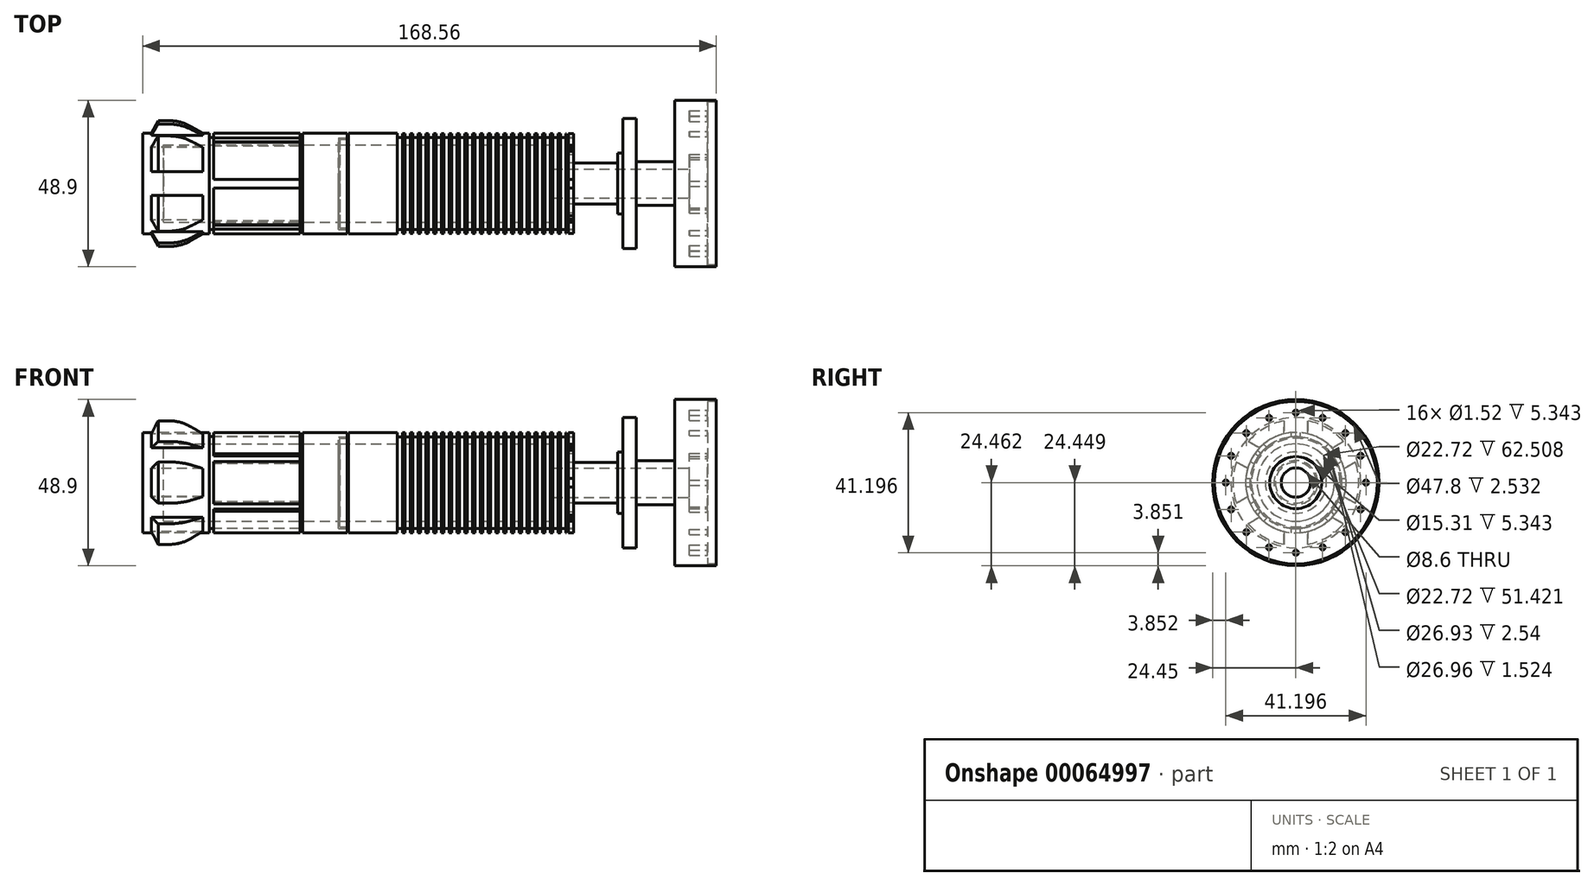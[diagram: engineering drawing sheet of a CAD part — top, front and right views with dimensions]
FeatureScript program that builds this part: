
annotation { "Feature Type Name" : "Feature", "Feature Type Description" : "" }
export const myFeature = defineFeature(function(context is Context, id is Id, definition is map)
    precondition{}
    {
        {
            var Q0;
            Q0=qCreatedBy(makeId("Front.planeOp"),FACE);
            var sketch = newSketch(context, id + "F0", { "sketchPlane" : qUnion([Q0])});
            skLineSegment(sketch, "E0", {"start": v(-51.18, 19.75) * mm, "end": v(-48.64, 19.75) * mm});
            skLineSegment(sketch, "E1", {"start": v(73.35, 19.75) * mm, "end": v(73.35, 28.51) * mm});
            skLineSegment(sketch, "E2", {"start": v(73.35, 28.51) * mm, "end": v(88.38, 28.51) * mm});
            skLineSegment(sketch, "E3", {"start": v(88.38, 28.51) * mm, "end": v(88.38, 25.51) * mm});
            skLineSegment(sketch, "E4", {"start": v(88.38, 25.51) * mm, "end": v(90, 25.51) * mm});
            skLineSegment(sketch, "E5", {"start": v(90, 25.51) * mm, "end": v(90, 15.36) * mm});
            skLineSegment(sketch, "E6", {"start": v(90, 15.36) * mm, "end": v(93.92, 15.36) * mm});
            skLineSegment(sketch, "E7", {"start": v(93.92, 15.36) * mm, "end": v(93.92, 28.05) * mm});
            skLineSegment(sketch, "E8", {"start": v(93.92, 28.05) * mm, "end": v(105.22, 28.05) * mm});
            skLineSegment(sketch, "E9", {"start": v(105.22, 28.05) * mm, "end": v(105.22, 10.06) * mm});
            skLineSegment(sketch, "E10", {"start": v(105.22, 10.06) * mm, "end": v(114.85, 10.06) * mm});
            skLineSegment(sketch, "E11", {"start": v(114.85, 10.6) * mm, "end": v(114.85, 27) * mm});
            skLineSegment(sketch, "E12", {"start": v(-51.18, 19.75) * mm, "end": v(-51.18, 28.51) * mm});
            skLineSegment(sketch, "E13", {"start": v(-51.18, 28.51) * mm, "end": v(-51.18, 34.5) * mm});
            skLineSegment(sketch, "E14", {"start": v(-51.18, 34.5) * mm, "end": v(114.85, 34.5) * mm});
            skLineSegment(sketch, "E15", {"start": v(114.85, 34.5) * mm, "end": v(114.85, 27) * mm});
            skLineSegment(sketch, "E16", {"start": v(114.85, 10.06) * mm, "end": v(117.38, 10.06) * mm});
            skLineSegment(sketch, "E17", {"start": v(117.38, 10.06) * mm, "end": v(117.38, 10.6) * mm});
            skLineSegment(sketch, "E18", {"start": v(117.38, 10.6) * mm, "end": v(114.85, 10.6) * mm});
            skLineSegment(sketch, "E19", {"start": v(-48.64, 19.75) * mm, "end": v(-46.64, 16.02) * mm});
            skLineSegment(sketch, "E20", {"start": v(-46.64, 16.02) * mm, "end": v(-39.86, 16.02) * mm});
            skLineSegment(sketch, "E21", {"start": v(-39.86, 16.02) * mm, "end": v(-33.55, 19.75) * mm});
            skLineSegment(sketch, "E22.trimOffspring", {"start": v(-33.55, 19.75) * mm, "end": v(-31.55, 19.75) * mm});
            skLineSegment(sketch, "E23", {"start": v(77.77, 19.75) * mm, "end": v(77.77, 21.03) * mm});
            skLineSegment(sketch, "E24", {"start": v(77.77, 21.03) * mm, "end": v(76.24, 21.03) * mm});
            skLineSegment(sketch, "E25", {"start": v(76.24, 21.03) * mm, "end": v(76.24, 19.75) * mm});
            skLineSegment(sketch, "E26.1.0.0", {"start": v(75.48, 19.75) * mm, "end": v(75.48, 21.03) * mm});
            skLineSegment(sketch, "E26.1.0.1", {"start": v(75.48, 21.03) * mm, "end": v(73.96, 21.03) * mm});
            skLineSegment(sketch, "E26.1.0.2", {"start": v(73.96, 21.03) * mm, "end": v(73.96, 19.75) * mm});
            skLineSegment(sketch, "E26.2.0.0", {"start": v(73.2, 19.75) * mm, "end": v(73.2, 21.03) * mm});
            skLineSegment(sketch, "E26.2.0.1", {"start": v(73.2, 21.03) * mm, "end": v(71.67, 21.03) * mm});
            skLineSegment(sketch, "E26.2.0.2", {"start": v(71.67, 21.03) * mm, "end": v(71.67, 19.75) * mm});
            skLineSegment(sketch, "E26.3.0.0", {"start": v(70.9, 19.75) * mm, "end": v(70.9, 21.03) * mm});
            skLineSegment(sketch, "E26.3.0.1", {"start": v(70.9, 21.03) * mm, "end": v(69.39, 21.03) * mm});
            skLineSegment(sketch, "E26.3.0.2", {"start": v(69.39, 21.03) * mm, "end": v(69.39, 19.75) * mm});
            skLineSegment(sketch, "E26.4.0.0", {"start": v(68.62, 19.75) * mm, "end": v(68.62, 21.03) * mm});
            skLineSegment(sketch, "E26.4.0.1", {"start": v(68.62, 21.03) * mm, "end": v(67.1, 21.03) * mm});
            skLineSegment(sketch, "E26.4.0.2", {"start": v(67.1, 21.03) * mm, "end": v(67.1, 19.75) * mm});
            skLineSegment(sketch, "E26.5.0.0", {"start": v(66.34, 19.75) * mm, "end": v(66.34, 21.03) * mm});
            skLineSegment(sketch, "E26.5.0.1", {"start": v(66.34, 21.03) * mm, "end": v(64.81, 21.03) * mm});
            skLineSegment(sketch, "E26.5.0.2", {"start": v(64.81, 21.03) * mm, "end": v(64.81, 19.75) * mm});
            skLineSegment(sketch, "E26.6.0.0", {"start": v(64.05, 19.75) * mm, "end": v(64.05, 21.03) * mm});
            skLineSegment(sketch, "E26.6.0.1", {"start": v(64.05, 21.03) * mm, "end": v(62.53, 21.03) * mm});
            skLineSegment(sketch, "E26.6.0.2", {"start": v(62.53, 21.03) * mm, "end": v(62.53, 19.75) * mm});
            skLineSegment(sketch, "E26.7.0.0", {"start": v(61.77, 19.75) * mm, "end": v(61.77, 21.03) * mm});
            skLineSegment(sketch, "E26.7.0.1", {"start": v(61.77, 21.03) * mm, "end": v(60.24, 21.03) * mm});
            skLineSegment(sketch, "E26.7.0.2", {"start": v(60.24, 21.03) * mm, "end": v(60.24, 19.75) * mm});
            skLineSegment(sketch, "E26.8.0.0", {"start": v(59.48, 19.75) * mm, "end": v(59.48, 21.03) * mm});
            skLineSegment(sketch, "E26.8.0.1", {"start": v(59.48, 21.03) * mm, "end": v(57.96, 21.03) * mm});
            skLineSegment(sketch, "E26.8.0.2", {"start": v(57.96, 21.03) * mm, "end": v(57.96, 19.75) * mm});
            skLineSegment(sketch, "E26.9.0.0", {"start": v(57.2, 19.75) * mm, "end": v(57.2, 21.03) * mm});
            skLineSegment(sketch, "E26.9.0.1", {"start": v(57.2, 21.03) * mm, "end": v(55.67, 21.03) * mm});
            skLineSegment(sketch, "E26.9.0.2", {"start": v(55.67, 21.03) * mm, "end": v(55.67, 19.75) * mm});
            skLineSegment(sketch, "E26.10.0.0", {"start": v(54.9, 19.75) * mm, "end": v(54.9, 21.03) * mm});
            skLineSegment(sketch, "E26.10.0.1", {"start": v(54.9, 21.03) * mm, "end": v(53.38, 21.03) * mm});
            skLineSegment(sketch, "E26.10.0.2", {"start": v(53.38, 21.03) * mm, "end": v(53.38, 19.75) * mm});
            skLineSegment(sketch, "E26.11.0.0", {"start": v(52.62, 19.75) * mm, "end": v(52.62, 21.03) * mm});
            skLineSegment(sketch, "E26.11.0.1", {"start": v(52.62, 21.03) * mm, "end": v(51.1, 21.03) * mm});
            skLineSegment(sketch, "E26.11.0.2", {"start": v(51.1, 21.03) * mm, "end": v(51.1, 19.75) * mm});
            skLineSegment(sketch, "E26.direction1", {"start": v(76.24, 19.75) * mm, "end": v(75.48, 19.75) * mm, "construction": true});
            skLineSegment(sketch, "E27.0.12.0", {"start": v(50.34, 19.75) * mm, "end": v(50.34, 21.03) * mm});
            skLineSegment(sketch, "E27.3.12.0", {"start": v(50.34, 21.03) * mm, "end": v(48.81, 21.03) * mm});
            skLineSegment(sketch, "E27.6.12.0", {"start": v(48.81, 21.03) * mm, "end": v(48.81, 19.75) * mm});
            skLineSegment(sketch, "E27.0.13.0", {"start": v(48.05, 19.75) * mm, "end": v(48.05, 21.03) * mm});
            skLineSegment(sketch, "E27.3.13.0", {"start": v(48.05, 21.03) * mm, "end": v(46.53, 21.03) * mm});
            skLineSegment(sketch, "E27.6.13.0", {"start": v(46.53, 21.03) * mm, "end": v(46.53, 19.75) * mm});
            skLineSegment(sketch, "E27.0.14.0", {"start": v(45.76, 19.75) * mm, "end": v(45.76, 21.03) * mm});
            skLineSegment(sketch, "E27.3.14.0", {"start": v(45.76, 21.03) * mm, "end": v(44.24, 21.03) * mm});
            skLineSegment(sketch, "E27.6.14.0", {"start": v(44.24, 21.03) * mm, "end": v(44.24, 19.75) * mm});
            skLineSegment(sketch, "E27.0.15.0", {"start": v(43.48, 19.75) * mm, "end": v(43.48, 21.03) * mm});
            skLineSegment(sketch, "E27.3.15.0", {"start": v(43.48, 21.03) * mm, "end": v(41.95, 21.03) * mm});
            skLineSegment(sketch, "E27.6.15.0", {"start": v(41.95, 21.03) * mm, "end": v(41.95, 19.75) * mm});
            skLineSegment(sketch, "E27.0.16.0", {"start": v(41.2, 19.75) * mm, "end": v(41.2, 21.03) * mm});
            skLineSegment(sketch, "E27.3.16.0", {"start": v(41.2, 21.03) * mm, "end": v(39.67, 21.03) * mm});
            skLineSegment(sketch, "E27.6.16.0", {"start": v(39.67, 21.03) * mm, "end": v(39.67, 19.75) * mm});
            skLineSegment(sketch, "E27.0.17.0", {"start": v(38.9, 19.75) * mm, "end": v(38.9, 21.03) * mm});
            skLineSegment(sketch, "E27.3.17.0", {"start": v(38.9, 21.03) * mm, "end": v(37.38, 21.03) * mm});
            skLineSegment(sketch, "E27.6.17.0", {"start": v(37.38, 21.03) * mm, "end": v(37.38, 19.75) * mm});
            skLineSegment(sketch, "E27.0.18.0", {"start": v(36.62, 19.75) * mm, "end": v(36.62, 21.03) * mm});
            skLineSegment(sketch, "E27.3.18.0", {"start": v(36.62, 21.03) * mm, "end": v(35.1, 21.03) * mm});
            skLineSegment(sketch, "E27.6.18.0", {"start": v(35.1, 21.03) * mm, "end": v(35.1, 19.75) * mm});
            skLineSegment(sketch, "E27.0.19.0", {"start": v(34.33, 19.75) * mm, "end": v(34.33, 21.03) * mm});
            skLineSegment(sketch, "E27.3.19.0", {"start": v(34.33, 21.03) * mm, "end": v(32.8, 21.03) * mm});
            skLineSegment(sketch, "E27.6.19.0", {"start": v(32.8, 21.03) * mm, "end": v(32.8, 19.75) * mm});
            skLineSegment(sketch, "E28.0.20.0", {"start": v(32.05, 19.75) * mm, "end": v(32.05, 21.03) * mm});
            skLineSegment(sketch, "E28.3.20.0", {"start": v(32.05, 21.03) * mm, "end": v(30.52, 21.03) * mm});
            skLineSegment(sketch, "E28.6.20.0", {"start": v(30.52, 21.03) * mm, "end": v(30.52, 19.75) * mm});
            skLineSegment(sketch, "E28.0.21.0", {"start": v(29.76, 19.75) * mm, "end": v(29.76, 21.03) * mm});
            skLineSegment(sketch, "E28.3.21.0", {"start": v(29.76, 21.03) * mm, "end": v(28.24, 21.03) * mm});
            skLineSegment(sketch, "E28.6.21.0", {"start": v(28.24, 21.03) * mm, "end": v(28.24, 19.75) * mm});
            skLineSegment(sketch, "E28.0.22.0", {"start": v(27.48, 19.75) * mm, "end": v(27.48, 21.03) * mm});
            skLineSegment(sketch, "E28.3.22.0", {"start": v(27.48, 21.03) * mm, "end": v(25.95, 21.03) * mm});
            skLineSegment(sketch, "E28.6.22.0", {"start": v(25.95, 21.03) * mm, "end": v(25.95, 19.75) * mm});
            skLineSegment(sketch, "E28.0.23.0", {"start": v(25.19, 19.75) * mm, "end": v(25.19, 21.03) * mm});
            skLineSegment(sketch, "E28.3.23.0", {"start": v(25.19, 21.03) * mm, "end": v(23.67, 21.03) * mm});
            skLineSegment(sketch, "E28.6.23.0", {"start": v(23.67, 21.03) * mm, "end": v(23.67, 19.75) * mm});
            skLineSegment(sketch, "E29.trimOffspring", {"start": v(73.35, 19.75) * mm, "end": v(77.77, 19.75) * mm});
            skLineSegment(sketch, "E30.trimOffspring", {"start": v(75.48, 19.75) * mm, "end": v(76.24, 19.75) * mm});
            skLineSegment(sketch, "E31.trimOffspring", {"start": v(73.2, 19.75) * mm, "end": v(73.96, 19.75) * mm});
            skLineSegment(sketch, "E32.trimOffspring", {"start": v(70.9, 19.75) * mm, "end": v(71.67, 19.75) * mm});
            skLineSegment(sketch, "E33.trimOffspring", {"start": v(68.62, 19.75) * mm, "end": v(69.39, 19.75) * mm});
            skLineSegment(sketch, "E34.trimOffspring", {"start": v(66.34, 19.75) * mm, "end": v(67.1, 19.75) * mm});
            skLineSegment(sketch, "E35.trimOffspring", {"start": v(64.05, 19.75) * mm, "end": v(64.81, 19.75) * mm});
            skLineSegment(sketch, "E36.trimOffspring", {"start": v(61.77, 19.75) * mm, "end": v(62.53, 19.75) * mm});
            skLineSegment(sketch, "E37.trimOffspring", {"start": v(59.48, 19.75) * mm, "end": v(60.24, 19.75) * mm});
            skLineSegment(sketch, "E38.trimOffspring", {"start": v(57.2, 19.75) * mm, "end": v(57.96, 19.75) * mm});
            skLineSegment(sketch, "E39.trimOffspring", {"start": v(52.62, 19.75) * mm, "end": v(53.38, 19.75) * mm});
            skLineSegment(sketch, "E40.trimOffspring", {"start": v(50.34, 19.75) * mm, "end": v(51.1, 19.75) * mm});
            skLineSegment(sketch, "E41.trimOffspring", {"start": v(48.05, 19.75) * mm, "end": v(48.81, 19.75) * mm});
            skLineSegment(sketch, "E42.trimOffspring", {"start": v(45.76, 19.75) * mm, "end": v(46.53, 19.75) * mm});
            skLineSegment(sketch, "E43.trimOffspring", {"start": v(43.48, 19.75) * mm, "end": v(44.24, 19.75) * mm});
            skLineSegment(sketch, "E44.trimOffspring", {"start": v(25.19, 19.75) * mm, "end": v(25.95, 19.75) * mm});
            skLineSegment(sketch, "E45.trimOffspring", {"start": v(27.48, 19.75) * mm, "end": v(28.24, 19.75) * mm});
            skLineSegment(sketch, "E46.trimOffspring", {"start": v(29.76, 19.75) * mm, "end": v(30.52, 19.75) * mm});
            skLineSegment(sketch, "E47.trimOffspring", {"start": v(34.33, 19.75) * mm, "end": v(35.1, 19.75) * mm});
            skLineSegment(sketch, "E48.trimOffspring", {"start": v(36.62, 19.75) * mm, "end": v(37.38, 19.75) * mm});
            skLineSegment(sketch, "E49.trimOffspring", {"start": v(38.9, 19.75) * mm, "end": v(39.67, 19.75) * mm});
            skLineSegment(sketch, "E50.trimOffspring", {"start": v(41.2, 19.75) * mm, "end": v(41.95, 19.75) * mm});
            skLineSegment(sketch, "E51", {"start": v(54.9, 19.75) * mm, "end": v(55.67, 19.75) * mm});
            skLineSegment(sketch, "E52", {"start": v(32.8, 19.75) * mm, "end": v(32.05, 19.75) * mm});
            skLineSegment(sketch, "E53.top", {"start": v(-31.55, 21.01) * mm, "end": v(-30.34, 21.01) * mm});
            skLineSegment(sketch, "E53.left", {"start": v(-31.55, 19.75) * mm, "end": v(-31.55, 21.01) * mm});
            skLineSegment(sketch, "E53.right", {"start": v(-30.34, 19.75) * mm, "end": v(-30.34, 21.01) * mm});
            skPoint(sketch, "E54.oppositeSnap0", {"position": v(-4.94, 19.75) * mm});
            skLineSegment(sketch, "E54.top", {"start": v(-4.18, 21.18) * mm, "end": v(-4.94, 21.18) * mm});
            skLineSegment(sketch, "E54.left", {"start": v(-4.18, 19.75) * mm, "end": v(-4.18, 21.18) * mm});
            skLineSegment(sketch, "E54.right", {"start": v(-4.94, 19.75) * mm, "end": v(-4.94, 21.18) * mm});
            skLineSegment(sketch, "E55.trimOffspring", {"start": v(-4.18, 19.75) * mm, "end": v(23.67, 19.75) * mm});
            skLineSegment(sketch, "E56.trimOffspring", {"start": v(-30.34, 19.75) * mm, "end": v(-4.94, 19.75) * mm});
            skSolve(sketch);
        }
        {
            var Q0;
            Q0 = qSketchRegion(id + "F0", true);
            var Q1;
            Q1=sQuery(id+"F0.wireOp",EDGE,"E14");
            revolve(context, id + "F1", {"entities" : qUnion([Q0]), "axis" : qUnion([Q1]), "revolveType" : RevolveType.FULL});
        }
        {
            var Q0;
            Q0=makeQuery(id+"F1.opRevolve","SWEPT_FACE",FACE,{"disambiguationData":[OSD([sQuery(id+"F0.wireOp",EDGE,"E12"),sQuery(id+"F0.wireOp",EDGE,"E13")])]});
            var sketch = newSketch(context, id + "F2", { "sketchPlane" : qUnion([Q0])});
            skLineSegment(sketch, "E57", {"start": v(-3.49, 60.37) * mm, "end": v(-3.49, 48.85) * mm});
            skLineSegment(sketch, "E58", {"start": v(3.46, 60.37) * mm, "end": v(3.46, 48.86) * mm});
            skArc(sketch, "E59", {"start": v(-10.7, 44.68) * mm, "mid": v(-12.8, 41.88) * mm, "end": v(-14.17, 38.66) * mm});
            skLineSegment(sketch, "E60.1.0", {"start": v(-24.14, 44.42) * mm, "end": v(-14.17, 38.66) * mm});
            skLineSegment(sketch, "E60.1.1", {"start": v(-20.67, 50.44) * mm, "end": v(-10.7, 44.68) * mm});
            skLineSegment(sketch, "E60.2.0", {"start": v(-20.65, 18.56) * mm, "end": v(-10.68, 24.32) * mm});
            skLineSegment(sketch, "E60.2.1", {"start": v(-24.13, 24.57) * mm, "end": v(-14.16, 30.33) * mm});
            skLineSegment(sketch, "E60.3.0", {"start": v(3.49, 8.65) * mm, "end": v(3.49, 20.16) * mm});
            skLineSegment(sketch, "E60.3.1", {"start": v(-3.46, 8.65) * mm, "end": v(-3.46, 20.16) * mm});
            skLineSegment(sketch, "E60.4.0", {"start": v(24.14, 24.6) * mm, "end": v(14.17, 30.36) * mm});
            skLineSegment(sketch, "E60.4.1", {"start": v(20.67, 18.58) * mm, "end": v(10.7, 24.34) * mm});
            skLineSegment(sketch, "E60.5.0", {"start": v(20.65, 50.46) * mm, "end": v(10.68, 44.7) * mm});
            skLineSegment(sketch, "E60.5.1", {"start": v(24.13, 44.44) * mm, "end": v(14.16, 38.69) * mm});
            skArc(sketch, "E61.trimOffspring", {"start": v(3.46, 48.86) * mm, "mid": v(-0.01, 49.27) * mm, "end": v(-3.49, 48.85) * mm});
            skArc(sketch, "E62.trimOffspring", {"start": v(14.16, 38.69) * mm, "mid": v(12.78, 41.9) * mm, "end": v(10.68, 44.7) * mm});
            skArc(sketch, "E63.trimOffspring", {"start": v(10.7, 24.34) * mm, "mid": v(12.8, 27.14) * mm, "end": v(14.17, 30.36) * mm});
            skArc(sketch, "E64.trimOffspring", {"start": v(-3.46, 20.16) * mm, "mid": v(0.01, 19.75) * mm, "end": v(3.49, 20.16) * mm});
            skArc(sketch, "E65.trimOffspring", {"start": v(-14.16, 30.33) * mm, "mid": v(-12.78, 27.11) * mm, "end": v(-10.68, 24.32) * mm});
            skLineSegment(sketch, "E66", {"start": v(-20.67, 50.44) * mm, "end": v(-24.14, 44.42) * mm});
            skLineSegment(sketch, "E67", {"start": v(-24.13, 24.57) * mm, "end": v(-20.65, 18.56) * mm});
            skLineSegment(sketch, "E68", {"start": v(-3.46, 8.65) * mm, "end": v(3.49, 8.65) * mm});
            skLineSegment(sketch, "E69", {"start": v(20.67, 18.58) * mm, "end": v(24.14, 24.6) * mm});
            skLineSegment(sketch, "E70", {"start": v(24.13, 44.44) * mm, "end": v(20.65, 50.46) * mm});
            skLineSegment(sketch, "E71", {"start": v(3.46, 60.37) * mm, "end": v(-3.49, 60.37) * mm});
            skSolve(sketch);
        }
        {
            var Q0;
            Q0=makeQuery(id+"F2.imprint","IMPRINT",FACE,{"disambiguationData":[TD([[makeQuery(id+"F2.imprint","IMPRINT",EDGE,{"derivedFrom":sQuery(id+"F2.wireOp",EDGE,"E57")}),1.0]])]});
            var Q1;
            Q1=makeQuery(id+"F2.imprint","IMPRINT",FACE,{"disambiguationData":[TD([[makeQuery(id+"F2.imprint","IMPRINT",EDGE,{"derivedFrom":sQuery(id+"F2.wireOp",EDGE,"E59")}),-1.0]])]});
            var Q2;
            Q2=makeQuery(id+"F2.imprint","IMPRINT",FACE,{"disambiguationData":[TD([[makeQuery(id+"F2.imprint","IMPRINT",EDGE,{"derivedFrom":sQuery(id+"F2.wireOp",EDGE,"E60.2.0")}),1.0]])]});
            var Q3;
            Q3=makeQuery(id+"F2.imprint","IMPRINT",FACE,{"disambiguationData":[TD([[makeQuery(id+"F2.imprint","IMPRINT",EDGE,{"derivedFrom":sQuery(id+"F2.wireOp",EDGE,"E60.3.0")}),1.0]])]});
            var Q4;
            Q4=makeQuery(id+"F2.imprint","IMPRINT",FACE,{"disambiguationData":[TD([[makeQuery(id+"F2.imprint","IMPRINT",EDGE,{"derivedFrom":sQuery(id+"F2.wireOp",EDGE,"E60.4.0")}),1.0]])]});
            var Q5;
            Q5=makeQuery(id+"F2.imprint","IMPRINT",FACE,{"disambiguationData":[TD([[makeQuery(id+"F2.imprint","IMPRINT",EDGE,{"derivedFrom":sQuery(id+"F2.wireOp",EDGE,"E60.5.0")}),1.0]])]});
            extrude(context, id + "F3", {"entities" : qUnion([Q0, Q1, Q2, Q3, Q4, Q5]), "operationType" : NewBodyOperationType.REMOVE, "oppositeDirection" : true, "depth" : 17.78 * mm});
        }
        {
            var Q0;
            {var subQ0=sQuery(id+"F0.wireOp",EDGE,"E20");var subQ1=sQuery(id+"F0.wireOp",EDGE,"E21");Q0=makeQuery(id+"F3.boolean.opBoolean","SPLIT",EDGE,{"disambiguationData":[TD([makeQuery(id+"F3.opExtrude","SWEPT_FACE",FACE,{"disambiguationData":[OSD([sQuery(id+"F2.wireOp",EDGE,"E60.2.0")])]})])],"derivedFrom":makeQuery(id+"F1.opRevolve","SWEPT_EDGE",EDGE,{"disambiguationData":[OSD([subQ0,subQ1])]})});}
            fillet(context, id + "F4", {"entities" : qUnion([Q0]), "radius" : 12.7 * mm, "tangentPropagation" : true, "allowEdgeOverflow" : false});
        }
        {
            var Q0;
            {var subQ0=sQuery(id+"F0.wireOp",EDGE,"E20");var subQ1=sQuery(id+"F0.wireOp",EDGE,"E21");Q0=makeQuery(id+"F3.boolean.opBoolean","SPLIT",EDGE,{"disambiguationData":[TD([makeQuery(id+"F3.opExtrude","SWEPT_FACE",FACE,{"disambiguationData":[OSD([sQuery(id+"F2.wireOp",EDGE,"E60.3.0")])]})])],"derivedFrom":makeQuery(id+"F1.opRevolve","SWEPT_EDGE",EDGE,{"disambiguationData":[OSD([subQ0,subQ1])]})});}
            fillet(context, id + "F5", {"entities" : qUnion([Q0]), "radius" : 12.7 * mm, "tangentPropagation" : true, "allowEdgeOverflow" : false});
        }
        {
            var Q0;
            {var subQ0=sQuery(id+"F0.wireOp",EDGE,"E20");var subQ1=sQuery(id+"F0.wireOp",EDGE,"E21");Q0=makeQuery(id+"F3.boolean.opBoolean","SPLIT",EDGE,{"disambiguationData":[TD([makeQuery(id+"F3.opExtrude","SWEPT_FACE",FACE,{"disambiguationData":[OSD([sQuery(id+"F2.wireOp",EDGE,"E60.4.0")])]})])],"derivedFrom":makeQuery(id+"F1.opRevolve","SWEPT_EDGE",EDGE,{"disambiguationData":[OSD([subQ0,subQ1])]})});}
            fillet(context, id + "F6", {"entities" : qUnion([Q0]), "radius" : 12.7 * mm, "tangentPropagation" : true, "allowEdgeOverflow" : false});
        }
        {
            var Q0;
            {var subQ0=sQuery(id+"F0.wireOp",EDGE,"E20");var subQ1=sQuery(id+"F0.wireOp",EDGE,"E21");Q0=makeQuery(id+"F3.boolean.opBoolean","SPLIT",EDGE,{"disambiguationData":[TD([makeQuery(id+"F3.opExtrude","SWEPT_FACE",FACE,{"disambiguationData":[OSD([sQuery(id+"F2.wireOp",EDGE,"E58")])]})])],"derivedFrom":makeQuery(id+"F1.opRevolve","SWEPT_EDGE",EDGE,{"disambiguationData":[OSD([subQ0,subQ1])]})});}
            fillet(context, id + "F7", {"entities" : qUnion([Q0]), "radius" : 12.7 * mm, "tangentPropagation" : true, "allowEdgeOverflow" : false});
        }
        {
            var Q0;
            {var subQ0=sQuery(id+"F0.wireOp",EDGE,"E20");var subQ1=sQuery(id+"F0.wireOp",EDGE,"E21");Q0=makeQuery(id+"F3.boolean.opBoolean","SPLIT",EDGE,{"disambiguationData":[TD([makeQuery(id+"F3.opExtrude","SWEPT_FACE",FACE,{"disambiguationData":[OSD([sQuery(id+"F2.wireOp",EDGE,"E57")])]})])],"derivedFrom":makeQuery(id+"F1.opRevolve","SWEPT_EDGE",EDGE,{"disambiguationData":[OSD([subQ0,subQ1])]})});}
            var Q1;
            {var subQ0=sQuery(id+"F0.wireOp",EDGE,"E20");var subQ1=sQuery(id+"F0.wireOp",EDGE,"E21");Q1=makeQuery(id+"F3.boolean.opBoolean","SPLIT",EDGE,{"disambiguationData":[TD([makeQuery(id+"F3.opExtrude","SWEPT_FACE",FACE,{"disambiguationData":[OSD([sQuery(id+"F2.wireOp",EDGE,"E60.1.0")])]})])],"derivedFrom":makeQuery(id+"F1.opRevolve","SWEPT_EDGE",EDGE,{"disambiguationData":[OSD([subQ0,subQ1])]})});}
            fillet(context, id + "F8", {"entities" : qUnion([Q0, Q1]), "radius" : 12.7 * mm, "tangentPropagation" : true, "allowEdgeOverflow" : false});
        }
        {
            var Q0;
            Q0=makeQuery(id+"F1.opRevolve","SWEPT_FACE",FACE,{"disambiguationData":[OSD([sQuery(id+"F0.wireOp",EDGE,"E25")])]});
            var sketch = newSketch(context, id + "F9", { "sketchPlane" : qUnion([Q0])});
            skArc(sketch, "E72.trimOffspring", {"start": v(1.27, 47.93) * mm, "mid": v(1.19, 47.94) * mm, "end": v(1.1, 47.95) * mm});
            skArc(sketch, "E73", {"start": v(-8.6, 44.9) * mm, "mid": v(-9.54, 44.05) * mm, "end": v(-10.4, 43.11) * mm});
            skArc(sketch, "E74", {"start": v(-16.55, 35.78) * mm, "mid": v(-16.6, 34.5) * mm, "end": v(-16.55, 33.24) * mm});
            skLineSegment(sketch, "E75", {"start": v(-1.27, 51.06) * mm, "end": v(-1.27, 47.94) * mm});
            skLineSegment(sketch, "E76", {"start": v(1.27, 47.93) * mm, "end": v(1.27, 51.06) * mm});
            skLineSegment(sketch, "E77.1.0", {"start": v(-8.6, 44.9) * mm, "end": v(-10.8, 47.11) * mm});
            skLineSegment(sketch, "E77.1.1", {"start": v(-12.6, 45.31) * mm, "end": v(-10.4, 43.11) * mm});
            skLineSegment(sketch, "E77.2.0", {"start": v(-13.42, 35.78) * mm, "end": v(-16.55, 35.78) * mm});
            skLineSegment(sketch, "E77.2.1", {"start": v(-16.55, 33.24) * mm, "end": v(-13.44, 33.24) * mm});
            skLineSegment(sketch, "E77.3.0", {"start": v(-10.39, 25.92) * mm, "end": v(-12.6, 23.7) * mm});
            skLineSegment(sketch, "E77.3.1", {"start": v(-10.8, 21.9) * mm, "end": v(-8.6, 24.11) * mm});
            skLineSegment(sketch, "E77.4.0", {"start": v(-1.27, 21.09) * mm, "end": v(-1.27, 17.96) * mm});
            skLineSegment(sketch, "E77.4.1", {"start": v(1.27, 17.96) * mm, "end": v(1.27, 21.07) * mm});
            skLineSegment(sketch, "E77.5.0", {"start": v(8.6, 24.12) * mm, "end": v(10.8, 21.9) * mm});
            skLineSegment(sketch, "E77.5.1", {"start": v(12.6, 23.7) * mm, "end": v(10.4, 25.9) * mm});
            skLineSegment(sketch, "E77.6.0", {"start": v(13.42, 33.24) * mm, "end": v(16.55, 33.24) * mm});
            skLineSegment(sketch, "E77.6.1", {"start": v(16.55, 35.78) * mm, "end": v(13.44, 35.78) * mm});
            skLineSegment(sketch, "E77.7.0", {"start": v(10.39, 43.1) * mm, "end": v(12.6, 45.31) * mm});
            skLineSegment(sketch, "E77.7.1", {"start": v(10.8, 47.11) * mm, "end": v(8.6, 44.9) * mm});
            skArc(sketch, "E78.trimOffspring", {"start": v(-10.8, 47.11) * mm, "mid": v(-11.74, 46.25) * mm, "end": v(-12.6, 45.31) * mm});
            skArc(sketch, "E79.trimOffspring", {"start": v(1.27, 51.06) * mm, "mid": v(0, 51.1) * mm, "end": v(-1.27, 51.06) * mm});
            skArc(sketch, "E80.trimOffspring", {"start": v(12.6, 45.31) * mm, "mid": v(11.74, 46.25) * mm, "end": v(10.8, 47.11) * mm});
            skArc(sketch, "E81.trimOffspring", {"start": v(-12.6, 23.7) * mm, "mid": v(-11.74, 22.77) * mm, "end": v(-10.8, 21.9) * mm});
            skArc(sketch, "E82.trimOffspring", {"start": v(-1.27, 17.96) * mm, "mid": v(0, 17.9) * mm, "end": v(1.27, 17.96) * mm});
            skArc(sketch, "E83.trimOffspring", {"start": v(10.8, 21.9) * mm, "mid": v(11.74, 22.77) * mm, "end": v(12.6, 23.7) * mm});
            skArc(sketch, "E84.trimOffspring", {"start": v(16.55, 33.24) * mm, "mid": v(16.6, 34.5) * mm, "end": v(16.55, 35.78) * mm});
            skArc(sketch, "E85.trimOffspring", {"start": v(-13.44, 35.78) * mm, "mid": v(-13.5, 34.5) * mm, "end": v(-13.44, 33.24) * mm});
            skArc(sketch, "E86.trimOffspring", {"start": v(-10.4, 25.9) * mm, "mid": v(-9.54, 24.97) * mm, "end": v(-8.6, 24.11) * mm});
            skArc(sketch, "E87.trimOffspring", {"start": v(-1.27, 21.07) * mm, "mid": v(0, 21.01) * mm, "end": v(1.27, 21.07) * mm});
            skArc(sketch, "E88.trimOffspring", {"start": v(8.6, 24.11) * mm, "mid": v(9.54, 24.97) * mm, "end": v(10.4, 25.9) * mm});
            skArc(sketch, "E89.trimOffspring", {"start": v(13.44, 33.24) * mm, "mid": v(13.5, 34.5) * mm, "end": v(13.44, 35.78) * mm});
            skArc(sketch, "E90.trimOffspring", {"start": v(10.4, 43.11) * mm, "mid": v(9.54, 44.05) * mm, "end": v(8.6, 44.9) * mm});
            skArc(sketch, "E91.trimOffspring", {"start": v(1.27, 47.94) * mm, "mid": v(0, 48) * mm, "end": v(-1.27, 47.94) * mm});
            skSolve(sketch);
        }
        {
            var Q0;
            Q0 = qSketchRegion(id + "F9", true);
            extrude(context, id + "F10", {"entities" : qUnion([Q0]), "operationType" : NewBodyOperationType.REMOVE, "depth" : 52.37 * mm});
        }
        {
            var Q0;
            Q0=makeQuery(id+"F1.opRevolve","SWEPT_FACE",FACE,{"disambiguationData":[OSD([sQuery(id+"F0.wireOp",EDGE,"E53.right")])]});
            var sketch = newSketch(context, id + "F11", { "sketchPlane" : qUnion([Q0])});
            skArc(sketch, "E92", {"start": v(-11, 42.33) * mm, "mid": v(-11.69, 41.26) * mm, "end": v(-12.27, 40.13) * mm});
            skArc(sketch, "E93", {"start": v(-13.37, 43.7) * mm, "mid": v(-14.04, 42.62) * mm, "end": v(-14.64, 41.5) * mm});
            skLineSegment(sketch, "E94", {"start": v(-1.27, 47.94) * mm, "end": v(-1.27, 50.68) * mm});
            skLineSegment(sketch, "E95", {"start": v(1.27, 50.68) * mm, "end": v(1.27, 47.94) * mm});
            skLineSegment(sketch, "E96.1.0", {"start": v(-13.37, 43.7) * mm, "end": v(-11, 42.33) * mm});
            skLineSegment(sketch, "E96.1.1", {"start": v(-12.27, 40.13) * mm, "end": v(-14.64, 41.5) * mm});
            skLineSegment(sketch, "E96.2.0", {"start": v(-14.64, 27.52) * mm, "end": v(-12.27, 28.9) * mm});
            skLineSegment(sketch, "E96.2.1", {"start": v(-11, 26.7) * mm, "end": v(-13.37, 25.33) * mm});
            skLineSegment(sketch, "E96.3.0", {"start": v(-1.27, 18.34) * mm, "end": v(-1.27, 21.07) * mm});
            skLineSegment(sketch, "E96.3.1", {"start": v(1.27, 21.07) * mm, "end": v(1.27, 18.34) * mm});
            skLineSegment(sketch, "E96.4.0", {"start": v(13.37, 25.33) * mm, "end": v(11, 26.7) * mm});
            skLineSegment(sketch, "E96.4.1", {"start": v(12.27, 28.9) * mm, "end": v(14.64, 27.52) * mm});
            skLineSegment(sketch, "E96.5.0", {"start": v(14.64, 41.5) * mm, "end": v(12.27, 40.13) * mm});
            skLineSegment(sketch, "E96.5.1", {"start": v(11, 42.33) * mm, "end": v(13.37, 43.7) * mm});
            skArc(sketch, "E97.trimOffspring", {"start": v(1.27, 47.94) * mm, "mid": v(0, 48) * mm, "end": v(-1.27, 47.94) * mm});
            skArc(sketch, "E98.trimOffspring", {"start": v(12.27, 40.13) * mm, "mid": v(11.69, 41.26) * mm, "end": v(11, 42.33) * mm});
            skArc(sketch, "E99.trimOffspring", {"start": v(11, 26.7) * mm, "mid": v(11.69, 27.76) * mm, "end": v(12.27, 28.9) * mm});
            skArc(sketch, "E100.trimOffspring", {"start": v(-1.27, 21.07) * mm, "mid": v(0, 21.01) * mm, "end": v(1.27, 21.07) * mm});
            skArc(sketch, "E101.trimOffspring", {"start": v(-12.27, 28.9) * mm, "mid": v(-11.69, 27.76) * mm, "end": v(-11, 26.7) * mm});
            skArc(sketch, "E102.trimOffspring", {"start": v(-14.64, 27.52) * mm, "mid": v(-14.04, 26.4) * mm, "end": v(-13.37, 25.33) * mm});
            skArc(sketch, "E103.trimOffspring", {"start": v(-1.27, 18.34) * mm, "mid": v(0, 18.3) * mm, "end": v(1.27, 18.34) * mm});
            skArc(sketch, "E104.trimOffspring", {"start": v(13.37, 25.33) * mm, "mid": v(14.04, 26.4) * mm, "end": v(14.64, 27.52) * mm});
            skArc(sketch, "E105.trimOffspring", {"start": v(14.64, 41.5) * mm, "mid": v(14.04, 42.62) * mm, "end": v(13.37, 43.7) * mm});
            skArc(sketch, "E106.trimOffspring", {"start": v(1.27, 50.68) * mm, "mid": v(0, 50.73) * mm, "end": v(-1.27, 50.68) * mm});
            skSolve(sketch);
        }
        {
            var Q0;
            Q0 = qSketchRegion(id + "F11", true);
            extrude(context, id + "F12", {"entities" : qUnion([Q0]), "operationType" : NewBodyOperationType.REMOVE, "oppositeDirection" : true, "depth" : 25.4 * mm});
        }
        {
            var Q0;
            Q0=makeQuery(id+"F1.opRevolve","SWEPT_FACE",FACE,{"disambiguationData":[OSD([sQuery(id+"F0.wireOp",EDGE,"E11"),sQuery(id+"F0.wireOp",EDGE,"E15")])]});
            var sketch = newSketch(context, id + "F13", { "sketchPlane" : qUnion([Q0])});
            skCircle(sketch, "E107", {"center": v(0, 55.1) * mm, "radius": 0.76 * mm});
            skCircle(sketch, "E108.1.0", {"center": v(-7.88, 53.54) * mm, "radius": 0.76 * mm});
            skCircle(sketch, "E108.2.0", {"center": v(-14.57, 49.07) * mm, "radius": 0.76 * mm});
            skCircle(sketch, "E108.3.0", {"center": v(-19.03, 42.4) * mm, "radius": 0.76 * mm});
            skCircle(sketch, "E108.4.0", {"center": v(-20.6, 34.5) * mm, "radius": 0.76 * mm});
            skCircle(sketch, "E108.5.0", {"center": v(-19.03, 26.63) * mm, "radius": 0.76 * mm});
            skCircle(sketch, "E108.6.0", {"center": v(-14.57, 19.94) * mm, "radius": 0.76 * mm});
            skCircle(sketch, "E108.7.0", {"center": v(-7.88, 15.48) * mm, "radius": 0.76 * mm});
            skCircle(sketch, "E108.8.0", {"center": v(0, 13.91) * mm, "radius": 0.76 * mm});
            skCircle(sketch, "E108.9.0", {"center": v(7.88, 15.48) * mm, "radius": 0.76 * mm});
            skCircle(sketch, "E108.10.0", {"center": v(14.57, 19.94) * mm, "radius": 0.76 * mm});
            skCircle(sketch, "E108.11.0", {"center": v(19.03, 26.63) * mm, "radius": 0.76 * mm});
            skCircle(sketch, "E108.12.0", {"center": v(20.6, 34.5) * mm, "radius": 0.76 * mm});
            skCircle(sketch, "E108.13.0", {"center": v(19.03, 42.4) * mm, "radius": 0.76 * mm});
            skCircle(sketch, "E108.14.0", {"center": v(14.57, 49.07) * mm, "radius": 0.76 * mm});
            skCircle(sketch, "E108.15.0", {"center": v(7.88, 53.54) * mm, "radius": 0.76 * mm});
            skPoint(sketch, "E108.center", {"position": v(0, 34.5) * mm});
            skCircle(sketch, "E109", {"center": v(0, 34.5) * mm, "radius": 7.66 * mm});
            skSolve(sketch);
        }
        {
            var Q0;
            Q0 = qSketchRegion(id + "F13", true);
            extrude(context, id + "F14", {"entities" : qUnion([Q0]), "operationType" : NewBodyOperationType.REMOVE, "oppositeDirection" : true, "depth" : 1.27 * mm});
        }
        {
            var Q0;
            Q0=makeQuery(id+"F1.opRevolve","SWEPT_BODY",BODY,{"disambiguationData":[OSD([sQuery(id+"F0.wireOp",EDGE,"E23"),sQuery(id+"F0.wireOp",EDGE,"E24"),sQuery(id+"F0.wireOp",EDGE,"E25"),sQuery(id+"F0.wireOp",EDGE,"E29.trimOffspring")])]});
            deleteBodies(context, id + "F15", {"entities" : qUnion([Q0])});
        }
        {
            var Q0;
            Q0 = qSketchRegion(id + "F13", true);
            extrude(context, id + "F16", {"entities" : qUnion([Q0]), "operationType" : NewBodyOperationType.REMOVE, "oppositeDirection" : true, "depth" : 5.34 * mm});
        }
        {
            var Q0;
            Q0=qCreatedBy(makeId("Front.planeOp"),FACE);
            var sketch = newSketch(context, id + "F17", { "sketchPlane" : qUnion([Q0])});
            skLineSegment(sketch, "E110.bottom", {"start": v(-45.1, 34.52) * mm, "end": v(69.27, 34.52) * mm});
            skLineSegment(sketch, "E110.top", {"start": v(-45.1, 23.16) * mm, "end": v(69.27, 23.16) * mm});
            skLineSegment(sketch, "E110.left", {"start": v(-45.1, 34.52) * mm, "end": v(-45.1, 23.16) * mm});
            skLineSegment(sketch, "E110.right", {"start": v(69.27, 30.22) * mm, "end": v(69.27, 23.16) * mm});
            skLineSegment(sketch, "E111.bottom", {"start": v(69.27, 34.52) * mm, "end": v(111.79, 34.52) * mm});
            skLineSegment(sketch, "E111.top", {"start": v(69.27, 30.22) * mm, "end": v(111.79, 30.22) * mm});
            skLineSegment(sketch, "E111.right", {"start": v(111.79, 34.52) * mm, "end": v(111.79, 30.22) * mm});
            skLineSegment(sketch, "E112", {"start": v(-33.55, 38.69) * mm, "end": v(-33.55, 30.36) * mm});
            skLineSegment(sketch, "E113", {"start": v(-33.55, 34.52) * mm, "end": v(-27.88, 34.52) * mm});
            skSolve(sketch);
        }
        {
            var Q0;
            Q0 = qSketchRegion(id + "F17", true);
            var Q1;
            Q1=sQuery(id+"F17.wireOp",EDGE,"E111.bottom");
            revolve(context, id + "F18", {"operationType" : NewBodyOperationType.REMOVE, "entities" : qUnion([Q0]), "axis" : qUnion([Q1]), "revolveType" : RevolveType.FULL, "oppositeDirection" : true});
        }
        {
            var Q0;
            Q0=qCreatedBy(makeId("Front.planeOp"),FACE);
            var sketch = newSketch(context, id + "F19", { "sketchPlane" : qUnion([Q0])});
            skLineSegment(sketch, "E114", {"start": v(9.3, 19.43) * mm, "end": v(9.3, 21.5) * mm});
            skLineSegment(sketch, "E115", {"start": v(9.3, 21.5) * mm, "end": v(6.77, 21.5) * mm});
            skLineSegment(sketch, "E116", {"start": v(6.77, 21.5) * mm, "end": v(6.77, 23.42) * mm});
            skLineSegment(sketch, "E117", {"start": v(6.77, 23.42) * mm, "end": v(6.32, 23.42) * mm});
            skLineSegment(sketch, "E118", {"start": v(6.32, 23.42) * mm, "end": v(6.32, 21.05) * mm});
            skLineSegment(sketch, "E119", {"start": v(6.32, 21.05) * mm, "end": v(8.86, 21.05) * mm});
            skLineSegment(sketch, "E120", {"start": v(8.86, 21.05) * mm, "end": v(8.86, 19.43) * mm});
            skLineSegment(sketch, "E121", {"start": v(8.86, 19.43) * mm, "end": v(9.3, 19.43) * mm});
            skLineSegment(sketch, "E122", {"start": v(-33.55, 38.69) * mm, "end": v(-33.55, 30.36) * mm});
            skLineSegment(sketch, "E123", {"start": v(-33.55, 34.52) * mm, "end": v(0, 34.52) * mm});
            skSolve(sketch);
        }
        {
            var Q0;
            Q0 = qSketchRegion(id + "F19", true);
            var Q1;
            Q1=sQuery(id+"F19.wireOp",EDGE,"E123");
            revolve(context, id + "F20", {"operationType" : NewBodyOperationType.REMOVE, "entities" : qUnion([Q0]), "axis" : qUnion([Q1]), "revolveType" : RevolveType.FULL, "oppositeDirection" : true});
        }
    });
